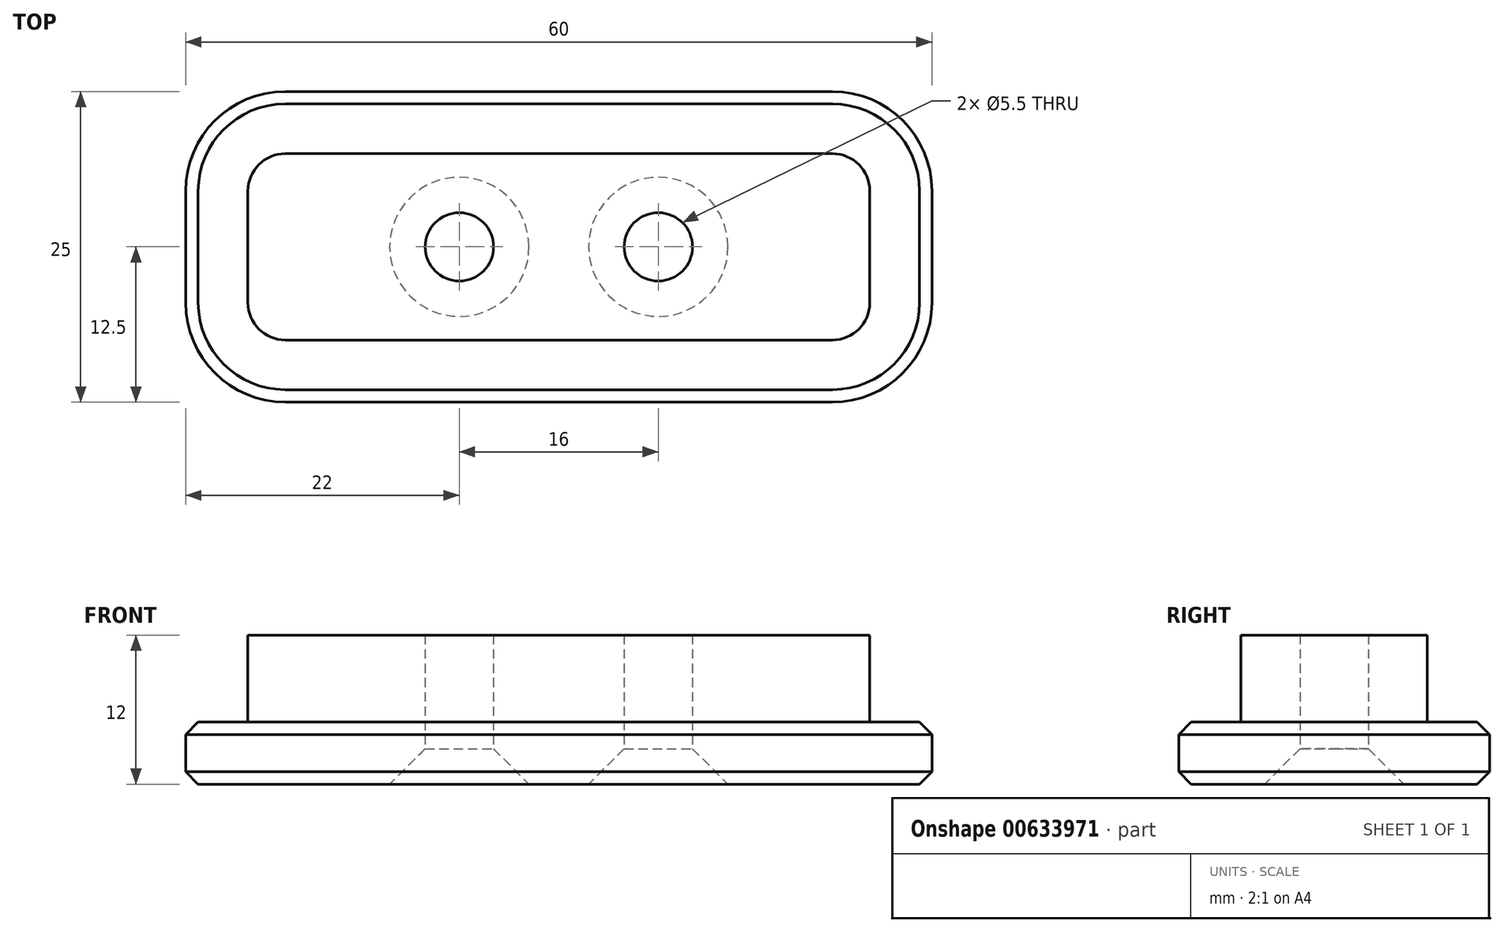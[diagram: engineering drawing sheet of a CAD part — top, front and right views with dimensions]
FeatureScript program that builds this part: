
annotation { "Feature Type Name" : "Feature", "Feature Type Description" : "" }
export const myFeature = defineFeature(function(context is Context, id is Id, definition is map)
    precondition{}
    {
        {
            var Q0;
            Q0=qCreatedBy(makeId("Top.planeOp"),FACE);
            var sketch = newSketch(context, id + "F0", { "sketchPlane" : qUnion([Q0])});
            skLineSegment(sketch, "E0.bottom", {"start": v(25, -7.5) * mm, "end": v(-25, -7.5) * mm});
            skLineSegment(sketch, "E0.top", {"start": v(25, 7.5) * mm, "end": v(-25, 7.5) * mm});
            skLineSegment(sketch, "E0.left", {"start": v(25, -7.5) * mm, "end": v(25, 7.5) * mm});
            skLineSegment(sketch, "E0.right", {"start": v(-25, -7.5) * mm, "end": v(-25, 7.5) * mm});
            skPoint(sketch, "E0.middle", {"position": v(0, 0) * mm});
            skSolve(sketch);
        }
        {
            var Q0;
            Q0=makeQuery(id+"F0.imprint","IMPRINT",FACE,{"disambiguationData":[TD([[makeQuery(id+"F0.imprint","IMPRINT",EDGE,{"derivedFrom":sQuery(id+"F0.wireOp",EDGE,"E0.bottom")}),-1.0]])]});
            extrude(context, id + "F1", {"entities" : qUnion([Q0]), "depth" : 7 * mm, "offsetDistance" : 25 * mm});
        }
        {
            var Q0;
            Q0=makeQuery(id+"F1.opExtrude","CAP_FACE",FACE,{"disambiguationData":[OSD([sQuery(id+"F0.wireOp",EDGE,"E0.bottom"),sQuery(id+"F0.wireOp",EDGE,"E0.top"),sQuery(id+"F0.wireOp",EDGE,"E0.left"),sQuery(id+"F0.wireOp",EDGE,"E0.right")])],"isStart":true});
            var sketch = newSketch(context, id + "F2", { "sketchPlane" : qUnion([Q0])});
            skLineSegment(sketch, "E1.bottom", {"start": v(30, 12.5) * mm, "end": v(-30, 12.5) * mm});
            skLineSegment(sketch, "E1.top", {"start": v(30, -12.5) * mm, "end": v(-30, -12.5) * mm});
            skLineSegment(sketch, "E1.left", {"start": v(30, 12.5) * mm, "end": v(30, -12.5) * mm});
            skLineSegment(sketch, "E1.right", {"start": v(-30, 12.5) * mm, "end": v(-30, -12.5) * mm});
            skPoint(sketch, "E1.middle", {"position": v(0, 0) * mm});
            skPoint(sketch, "E1.middle.positionSnap0", {"position": v(-25, 0) * mm});
            skPoint(sketch, "E1.middle.positionSnap1", {"position": v(0, -7.5) * mm});
            skPoint(sketch, "E1.centerSnap0", {"position": v(-25, 0) * mm});
            skPoint(sketch, "E1.centerSnap1", {"position": v(0, -7.5) * mm});
            skSolve(sketch);
        }
        {
            var Q0;
            Q0=makeQuery(id+"F2.imprint","IMPRINT",FACE,{"disambiguationData":[TD([[makeQuery(id+"F2.imprint","IMPRINT",EDGE,{"derivedFrom":makeQuery(id+"F1.opExtrude","CAP_EDGE",EDGE,{"disambiguationData":[OSD([sQuery(id+"F0.wireOp",EDGE,"E0.bottom")])],"isStart":true})}),1.0]])]});
            var Q1;
            Q1=makeQuery(id+"F2.imprint","IMPRINT",FACE,{"disambiguationData":[TD([[makeQuery(id+"F2.imprint","IMPRINT",EDGE,{"derivedFrom":sQuery(id+"F2.wireOp",EDGE,"E1.bottom")}),1.0]])]});
            extrude(context, id + "F3", {"entities" : qUnion([Q0, Q1]), "operationType" : NewBodyOperationType.ADD, "depth" : 5 * mm, "offsetDistance" : 25 * mm});
        }
        {
            var Q0;
            Q0=makeQuery(id+"F3.opExtrude","CAP_FACE",FACE,{"disambiguationData":[OSD([sQuery(id+"F2.wireOp",EDGE,"E1.bottom"),sQuery(id+"F2.wireOp",EDGE,"E1.top"),sQuery(id+"F2.wireOp",EDGE,"E1.left"),sQuery(id+"F2.wireOp",EDGE,"E1.right")])],"isStart":false});
            var sketch = newSketch(context, id + "F4", { "sketchPlane" : qUnion([Q0])});
            skLineSegment(sketch, "E2", {"start": v(0, 12.5) * mm, "end": v(0, -12.5) * mm, "construction": true});
            skLineSegment(sketch, "E3", {"start": v(-8, 0) * mm, "end": v(8, 0) * mm, "construction": true});
            skPoint(sketch, "E4", {"position": v(0, 0) * mm});
            skSolve(sketch);
        }
        {
            var Q0;
            Q0=sQuery(id+"F4.wireOp",VERTEX,"E3.start");
            var Q1;
            Q1=sQuery(id+"F4.wireOp",VERTEX,"E3.end");
            var Q2;
            Q2=makeQuery(id+"F1.opExtrude","SWEPT_BODY",BODY,{"disambiguationData":[OSD([sQuery(id+"F0.wireOp",EDGE,"E0.bottom"),sQuery(id+"F0.wireOp",EDGE,"E0.top"),sQuery(id+"F0.wireOp",EDGE,"E0.left"),sQuery(id+"F0.wireOp",EDGE,"E0.right")])]});
            hole(context, id + "F5", {"style" : HoleStyle.C_SINK, "endStyle" : HoleEndStyle.THROUGH, "standardTappedOrClearance" : lookupTablePath({ "standard" : "ISO", "fit" : "Normal", "size" : "M5", "type" : "Clearance" }), "standardBlindInLast" : lookupTablePath({ "fit" : "Standard", "standard" : "ISO", "size" : "M5", "type" : "Clearance" }), "holeDiameter" : 5.5 * mm, "cSinkDiameter" : 11.2 * mm, "cSinkAngle" : 90 * degree, "majorDiameter" : 5 * mm, "isTappedThrough" : true, "tappedDepth" : 12 * mm, "tapClearance" : 3, "locations" : qUnion([Q0, Q1]), "scope" : qUnion([Q2])});
        }
        {
            var Q0;
            Q0=makeQuery(id+"F3.opExtrude","SWEPT_EDGE",EDGE,{"disambiguationData":[OSD([sQuery(id+"F2.wireOp",EDGE,"E1.bottom"),sQuery(id+"F2.wireOp",EDGE,"E1.right")])]});
            var Q1;
            Q1=makeQuery(id+"F3.opExtrude","SWEPT_EDGE",EDGE,{"disambiguationData":[OSD([sQuery(id+"F2.wireOp",EDGE,"E1.top"),sQuery(id+"F2.wireOp",EDGE,"E1.right")])]});
            var Q2;
            Q2=makeQuery(id+"F3.opExtrude","SWEPT_EDGE",EDGE,{"disambiguationData":[OSD([sQuery(id+"F2.wireOp",EDGE,"E1.bottom"),sQuery(id+"F2.wireOp",EDGE,"E1.left")])]});
            var Q3;
            Q3=makeQuery(id+"F3.opExtrude","SWEPT_EDGE",EDGE,{"disambiguationData":[OSD([sQuery(id+"F2.wireOp",EDGE,"E1.top"),sQuery(id+"F2.wireOp",EDGE,"E1.left")])]});
            fillet(context, id + "F6", {"entities" : qUnion([Q0, Q1, Q2, Q3]), "radius" : 8 * mm, "tangentPropagation" : true, "allowEdgeOverflow" : false});
        }
        {
            var Q0;
            Q0=makeQuery(id+"F1.opExtrude","SWEPT_EDGE",EDGE,{"disambiguationData":[OSD([sQuery(id+"F0.wireOp",EDGE,"E0.bottom"),sQuery(id+"F0.wireOp",EDGE,"E0.left")])]});
            var Q1;
            Q1=makeQuery(id+"F1.opExtrude","SWEPT_EDGE",EDGE,{"disambiguationData":[OSD([sQuery(id+"F0.wireOp",EDGE,"E0.top"),sQuery(id+"F0.wireOp",EDGE,"E0.left")])]});
            var Q2;
            Q2=makeQuery(id+"F1.opExtrude","SWEPT_EDGE",EDGE,{"disambiguationData":[OSD([sQuery(id+"F0.wireOp",EDGE,"E0.top"),sQuery(id+"F0.wireOp",EDGE,"E0.right")])]});
            var Q3;
            Q3=makeQuery(id+"F1.opExtrude","SWEPT_EDGE",EDGE,{"disambiguationData":[OSD([sQuery(id+"F0.wireOp",EDGE,"E0.bottom"),sQuery(id+"F0.wireOp",EDGE,"E0.right")])]});
            fillet(context, id + "F7", {"entities" : qUnion([Q0, Q1, Q2, Q3]), "radius" : 3 * mm, "tangentPropagation" : true, "allowEdgeOverflow" : false});
        }
        {
            var Q0;
            Q0=makeQuery(id+"F3.opExtrude","CAP_EDGE",EDGE,{"disambiguationData":[OSD([sQuery(id+"F2.wireOp",EDGE,"E1.bottom")])],"isStart":false});
            var Q1;
            Q1=makeQuery(id+"F3.opExtrude","CAP_EDGE",EDGE,{"disambiguationData":[OSD([sQuery(id+"F2.wireOp",EDGE,"E1.left")])],"isStart":false});
            var Q2;
            Q2=makeQuery(id+"F3.opExtrude","CAP_EDGE",EDGE,{"disambiguationData":[OSD([sQuery(id+"F2.wireOp",EDGE,"E1.top")])],"isStart":false});
            var Q3;
            Q3=makeQuery(id+"F3.opExtrude","CAP_EDGE",EDGE,{"disambiguationData":[OSD([sQuery(id+"F2.wireOp",EDGE,"E1.right")])],"isStart":false});
            var Q4;
            Q4=makeQuery(id+"F3.opExtrude","CAP_EDGE",EDGE,{"disambiguationData":[OSD([sQuery(id+"F2.wireOp",EDGE,"E1.right")])],"isStart":true});
            var Q5;
            Q5=makeQuery(id+"F3.opExtrude","CAP_EDGE",EDGE,{"disambiguationData":[OSD([sQuery(id+"F2.wireOp",EDGE,"E1.top")])],"isStart":true});
            var Q6;
            Q6=makeQuery(id+"F3.opExtrude","CAP_EDGE",EDGE,{"disambiguationData":[OSD([sQuery(id+"F2.wireOp",EDGE,"E1.left")])],"isStart":true});
            var Q7;
            Q7=makeQuery(id+"F3.opExtrude","CAP_EDGE",EDGE,{"disambiguationData":[OSD([sQuery(id+"F2.wireOp",EDGE,"E1.bottom")])],"isStart":true});
            chamfer(context, id + "F8", {"entities" : qUnion([Q0, Q1, Q2, Q3, Q4, Q5, Q6, Q7]), "width" : 1 * mm, "tangentPropagation" : true});
        }
    });
